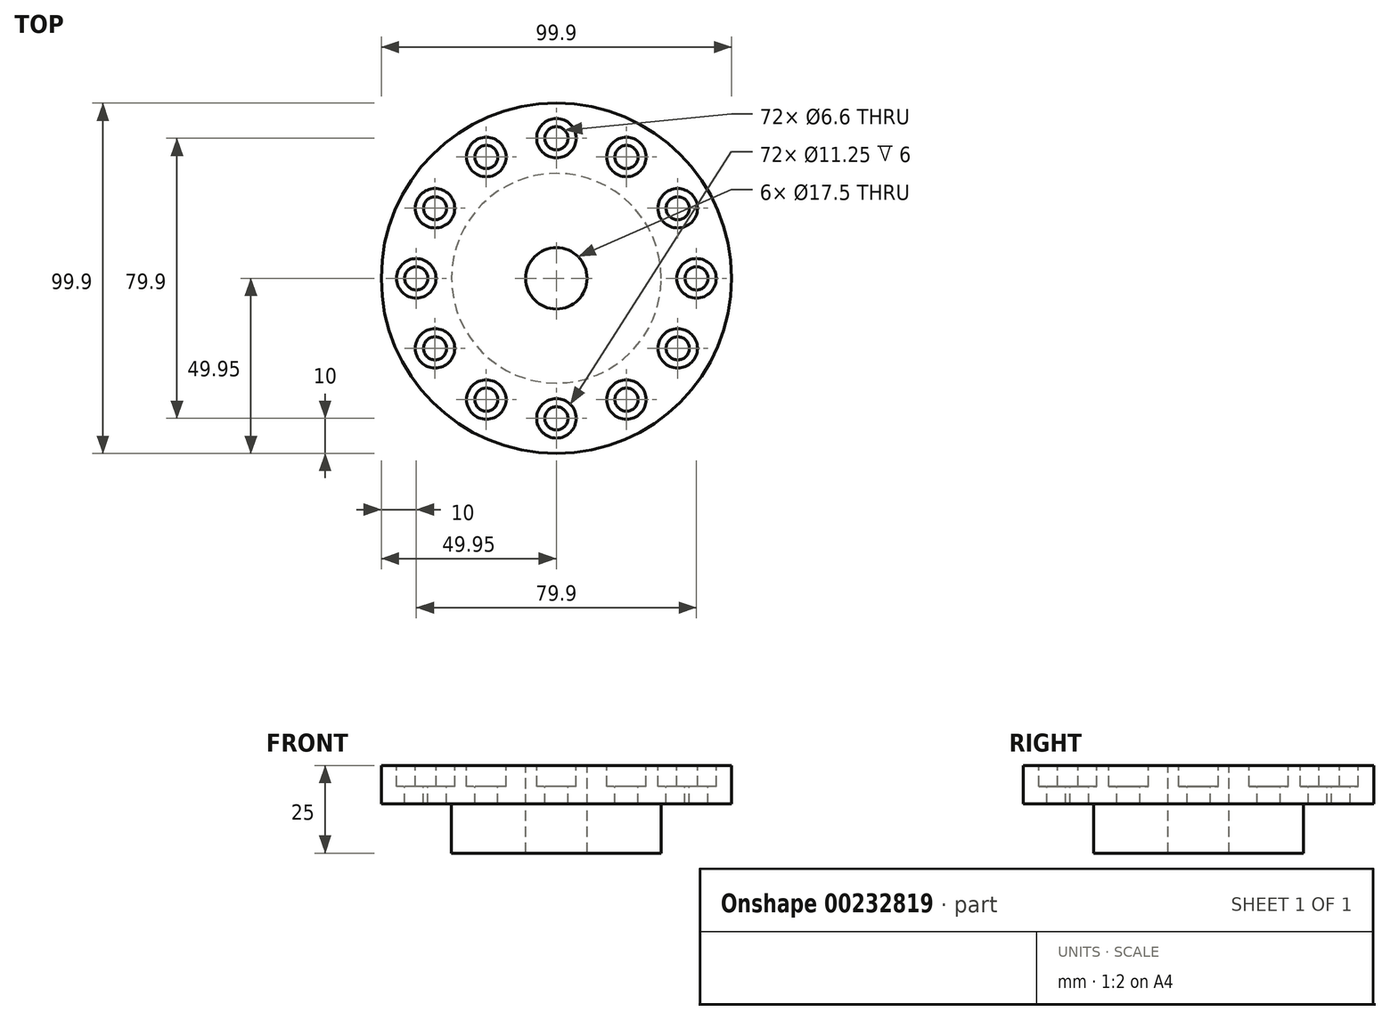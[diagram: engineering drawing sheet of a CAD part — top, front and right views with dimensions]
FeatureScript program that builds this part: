
annotation { "Feature Type Name" : "Feature", "Feature Type Description" : "" }
export const myFeature = defineFeature(function(context is Context, id is Id, definition is map)
    precondition{}
    {
        {
            var Q0;
            Q0=qCreatedBy(makeId("Front.planeOp"),FACE);
            var sketch = newSketch(context, id + "F0", { "sketchPlane" : qUnion([Q0])});
            skLineSegment(sketch, "E0", {"start": v(-29.9, 0) * mm, "end": v(-29.9, 14) * mm});
            skLineSegment(sketch, "E1", {"start": v(-29.9, 14) * mm, "end": v(-49.95, 14) * mm});
            skLineSegment(sketch, "E2", {"start": v(-49.95, 14) * mm, "end": v(-49.95, 25) * mm});
            skLineSegment(sketch, "E3", {"start": v(-49.95, 25) * mm, "end": v(0, 25) * mm});
            skLineSegment(sketch, "E4", {"start": v(0, 25) * mm, "end": v(0, 0) * mm});
            skLineSegment(sketch, "E5", {"start": v(0, 0) * mm, "end": v(-29.9, 0) * mm});
            skSolve(sketch);
        }
        {
            var Q0;
            Q0 = qSketchRegion(id + "F0", true);
            var Q1;
            Q1=sQuery(id+"F0.wireOp",EDGE,"E4");
            revolve(context, id + "F1", {"entities" : qUnion([Q0]), "axis" : qUnion([Q1]), "revolveType" : RevolveType.FULL});
        }
        {
            var Q0;
            Q0=makeQuery(id+"F1.opRevolve","SWEPT_FACE",FACE,{"disambiguationData":[OSD([sQuery(id+"F0.wireOp",EDGE,"E3")])]});
            var sketch = newSketch(context, id + "F2", { "sketchPlane" : qUnion([Q0])});
            skPoint(sketch, "E6", {"position": v(0, 39.95) * mm});
            skPoint(sketch, "E7.1.0", {"position": v(-19.97, 34.6) * mm});
            skPoint(sketch, "E7.2.0", {"position": v(-34.6, 19.98) * mm});
            skPoint(sketch, "E7.3.0", {"position": v(-39.95, 0) * mm});
            skPoint(sketch, "E7.4.0", {"position": v(-34.6, -19.97) * mm});
            skPoint(sketch, "E7.5.0", {"position": v(-19.97, -34.6) * mm});
            skPoint(sketch, "E7.6.0", {"position": v(0, -39.95) * mm});
            skPoint(sketch, "E7.7.0", {"position": v(19.97, -34.6) * mm});
            skPoint(sketch, "E7.8.0", {"position": v(34.6, -19.98) * mm});
            skPoint(sketch, "E7.9.0", {"position": v(39.95, 0) * mm});
            skPoint(sketch, "E7.10.0", {"position": v(34.6, 19.98) * mm});
            skPoint(sketch, "E7.11.0", {"position": v(19.98, 34.6) * mm});
            skPoint(sketch, "E7.center", {"position": v(0, 0) * mm});
            skSolve(sketch);
        }
        {
            var Q0;
            Q0=sQuery(id+"F2.wireOp",VERTEX,"E7.7.0");
            var Q1;
            Q1=sQuery(id+"F2.wireOp",VERTEX,"E7.9.0");
            var Q2;
            Q2=sQuery(id+"F2.wireOp",VERTEX,"E7.10.0");
            var Q3;
            Q3=sQuery(id+"F2.wireOp",VERTEX,"E7.8.0");
            var Q4;
            Q4=sQuery(id+"F2.wireOp",VERTEX,"E7.11.0");
            var Q5;
            Q5=sQuery(id+"F2.wireOp",VERTEX,"E6");
            var Q6;
            Q6=sQuery(id+"F2.wireOp",VERTEX,"E7.1.0");
            var Q7;
            Q7=sQuery(id+"F2.wireOp",VERTEX,"E7.2.0");
            var Q8;
            Q8=sQuery(id+"F2.wireOp",VERTEX,"E7.3.0");
            var Q9;
            Q9=sQuery(id+"F2.wireOp",VERTEX,"E7.4.0");
            var Q10;
            Q10=sQuery(id+"F2.wireOp",VERTEX,"E7.5.0");
            var Q11;
            Q11=sQuery(id+"F2.wireOp",VERTEX,"E7.6.0");
            var Q12;
            Q12=makeQuery(id+"F1.opRevolve","SWEPT_BODY",BODY,{"disambiguationData":[OSD([sQuery(id+"F0.wireOp",EDGE,"E0"),sQuery(id+"F0.wireOp",EDGE,"E1"),sQuery(id+"F0.wireOp",EDGE,"E2"),sQuery(id+"F0.wireOp",EDGE,"E3"),sQuery(id+"F0.wireOp",EDGE,"E4"),sQuery(id+"F0.wireOp",EDGE,"E5")])]});
            hole(context, id + "F3", {"style" : HoleStyle.C_BORE, "endStyle" : HoleEndStyle.BLIND, "standardTappedOrClearance" : lookupTablePath({ "standard" : "ISO", "fit" : "Normal", "size" : "M6", "type" : "Clearance" }), "standardBlindInLast" : lookupTablePath({ "fit" : "Standard", "standard" : "ISO", "size" : "M6", "type" : "Clearance" }), "holeDiameter" : 6.6 * mm, "cBoreDiameter" : 11.25 * mm, "cBoreDepth" : 6 * mm, "holeDepth" : 35 * mm, "tappedDepth" : 32 * mm, "tapClearance" : 3, "startFromSketch" : true, "locations" : qUnion([Q0, Q1, Q2, Q3, Q4, Q5, Q6, Q7, Q8, Q9, Q10, Q11]), "scope" : qUnion([Q12])});
        }
        {
            var Q0;
            Q0=makeQuery(id+"F1.opRevolve","SWEPT_FACE",FACE,{"disambiguationData":[OSD([sQuery(id+"F0.wireOp",EDGE,"E3")])]});
            var sketch = newSketch(context, id + "F4", { "sketchPlane" : qUnion([Q0])});
            skPoint(sketch, "E8", {"position": v(0, 0) * mm});
            skSolve(sketch);
        }
        {
            var Q0;
            Q0=sQuery(id+"F4.wireOp",VERTEX,"E8");
            var Q1;
            Q1=makeQuery(id+"F1.opRevolve","SWEPT_BODY",BODY,{"disambiguationData":[OSD([sQuery(id+"F0.wireOp",EDGE,"E0"),sQuery(id+"F0.wireOp",EDGE,"E1"),sQuery(id+"F0.wireOp",EDGE,"E2"),sQuery(id+"F0.wireOp",EDGE,"E3"),sQuery(id+"F0.wireOp",EDGE,"E4"),sQuery(id+"F0.wireOp",EDGE,"E5")])]});
            hole(context, id + "F5", {"style" : HoleStyle.SIMPLE, "endStyle" : HoleEndStyle.BLIND, "standardTappedOrClearance" : lookupTablePath({ "standard" : "ISO", "engagement" : "75%", "pitch" : "2.5 mm", "size" : "M20", "type" : "Tapped" }), "standardBlindInLast" : lookupTablePath({ "standard" : "ISO", "engagement" : "75%", "pitch" : "2.5 mm", "size" : "M20", "type" : "Tapped" }), "holeDiameter" : 17.5 * mm, "showTappedDepth" : true, "holeDepth" : 39.5 * mm, "tappedDepth" : 32 * mm, "tapClearance" : 3, "startFromSketch" : true, "locations" : qUnion([Q0]), "scope" : qUnion([Q1]), "majorDiameter" : 20 * mm});
        }
    });
